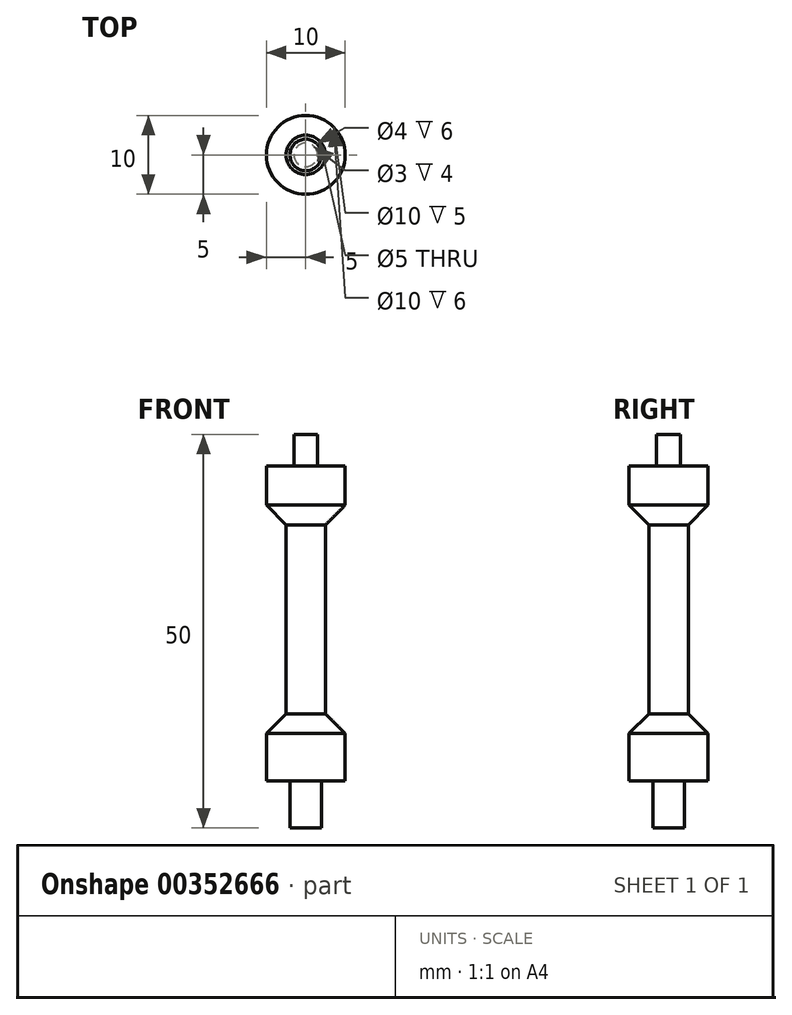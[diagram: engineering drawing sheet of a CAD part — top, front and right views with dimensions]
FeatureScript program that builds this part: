
annotation { "Feature Type Name" : "Feature", "Feature Type Description" : "" }
export const myFeature = defineFeature(function(context is Context, id is Id, definition is map)
    precondition{}
    {
        {
            var Q0;
            Q0=qCreatedBy(makeId("Right.planeOp"),FACE);
            var sketch = newSketch(context, id + "F0", { "sketchPlane" : qUnion([Q0])});
            skLineSegment(sketch, "E0", {"start": v(0, 0) * mm, "end": v(0, 43) * mm, "construction": true});
            skLineSegment(sketch, "E1", {"start": v(0, -6) * mm, "end": v(2, -6) * mm});
            skLineSegment(sketch, "E2", {"start": v(2, -6) * mm, "end": v(2, 0) * mm});
            skLineSegment(sketch, "E3", {"start": v(2, 0) * mm, "end": v(5, 0) * mm});
            skLineSegment(sketch, "E4", {"start": v(5, 0) * mm, "end": v(5, 6) * mm});
            skLineSegment(sketch, "E5", {"start": v(5, 6) * mm, "end": v(2.5, 8.5) * mm});
            skLineSegment(sketch, "E6", {"start": v(2.5, 8.5) * mm, "end": v(2.5, 32.5) * mm});
            skLineSegment(sketch, "E7", {"start": v(2.5, 32.5) * mm, "end": v(5, 35) * mm});
            skLineSegment(sketch, "E8", {"start": v(5, 35) * mm, "end": v(5, 40) * mm});
            skLineSegment(sketch, "E9", {"start": v(5, 40) * mm, "end": v(1.5, 40) * mm});
            skLineSegment(sketch, "E10", {"start": v(1.5, 40) * mm, "end": v(1.5, 44) * mm});
            skLineSegment(sketch, "E11", {"start": v(1.5, 44) * mm, "end": v(0, 44) * mm});
            skSolve(sketch);
        }
        {
            var Q0;
            Q0=sQuery(id+"F0.wireOp",EDGE,"E8");
            var Q1;
            Q1=sQuery(id+"F0.wireOp",EDGE,"E6");
            var Q2;
            Q2=sQuery(id+"F0.wireOp",EDGE,"E7");
            var Q3;
            Q3=sQuery(id+"F0.wireOp",EDGE,"E4");
            var Q4;
            Q4=sQuery(id+"F0.wireOp",EDGE,"E9");
            var Q5;
            Q5=sQuery(id+"F0.wireOp",EDGE,"E10");
            var Q6;
            Q6=sQuery(id+"F0.wireOp",EDGE,"E3");
            var Q7;
            Q7=sQuery(id+"F0.wireOp",EDGE,"E2");
            var Q8;
            Q8=sQuery(id+"F0.wireOp",EDGE,"E11");
            var Q9;
            Q9=sQuery(id+"F0.wireOp",EDGE,"E1");
            var Q10;
            Q10=sQuery(id+"F0.wireOp",EDGE,"E5");
            var Q11;
            Q11=sQuery(id+"F0.wireOp",EDGE,"E0");
            revolve(context, id + "F1", {"bodyType" : ToolBodyType.SURFACE, "surfaceEntities" : qUnion([Q0, Q1, Q2, Q3, Q4, Q5, Q6, Q7, Q8, Q9, Q10]), "axis" : qUnion([Q11]), "revolveType" : RevolveType.FULL});
        }
    });
